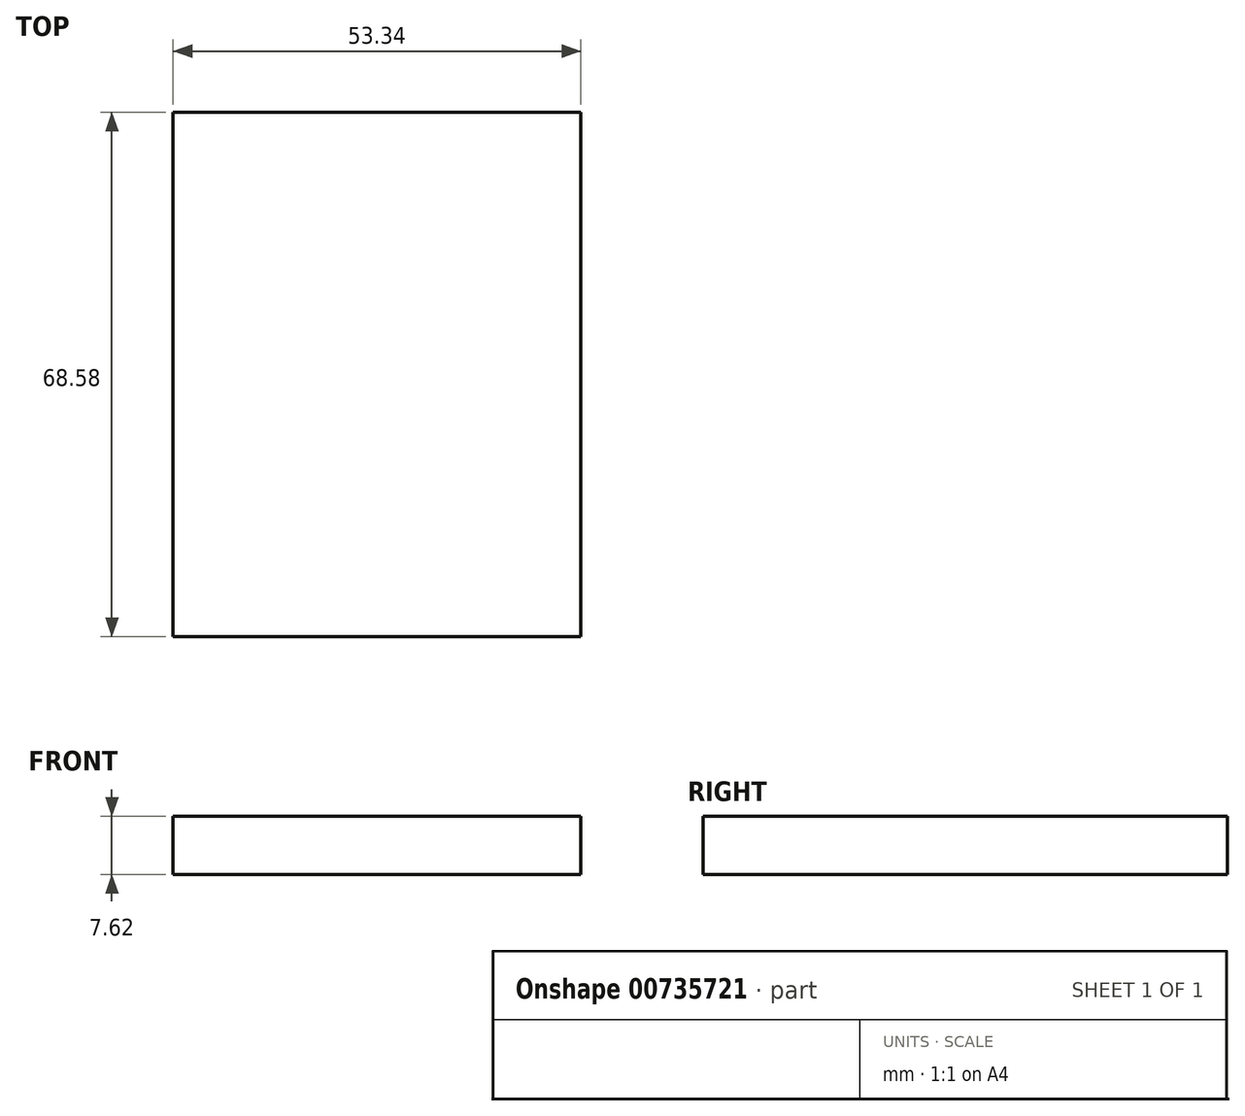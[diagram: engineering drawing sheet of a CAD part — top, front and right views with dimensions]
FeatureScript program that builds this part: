
annotation { "Feature Type Name" : "Feature", "Feature Type Description" : "" }
export const myFeature = defineFeature(function(context is Context, id is Id, definition is map)
    precondition{}
    {
        {
            var Q0;
            Q0=qCreatedBy(makeId("Top.planeOp"),FACE);
            var sketch = newSketch(context, id + "F0", { "sketchPlane" : qUnion([Q0])});
            skLineSegment(sketch, "E0", {"start": v(-26.67, 0) * mm, "end": v(0, 0) * mm});
            skLineSegment(sketch, "E1", {"start": v(0, 0) * mm, "end": v(0, 34.42) * mm});
            skLineSegment(sketch, "E2.MirrorCS", {"start": v(26.67, 0) * mm, "end": v(0, 0) * mm});
            skLineSegment(sketch, "E3.MirrorCS", {"start": v(0, 0) * mm, "end": v(0, -34.42) * mm});
            skLineSegment(sketch, "E4.bottom", {"start": v(-26.67, 34.42) * mm, "end": v(26.67, 34.42) * mm});
            skLineSegment(sketch, "E4.top", {"start": v(-26.67, -34.16) * mm, "end": v(26.67, -34.16) * mm});
            skLineSegment(sketch, "E4.left", {"start": v(-26.67, 34.42) * mm, "end": v(-26.67, -34.16) * mm});
            skLineSegment(sketch, "E4.right", {"start": v(26.67, 34.42) * mm, "end": v(26.67, -34.16) * mm});
            skSolve(sketch);
        }
        {
            var Q0;
            {var subQ0=sQuery(id+"F0.wireOp",EDGE,"E0");Q0=makeQuery(id+"F0.imprint","IMPRINT",FACE,{"disambiguationData":[TD([[makeQuery(id+"F0.imprint","IMPRINT",EDGE,{"derivedFrom":subQ0}),1.0]])]});}
            var Q1;
            {var subQ0=sQuery(id+"F0.wireOp",EDGE,"E1");Q1=makeQuery(id+"F0.imprint","IMPRINT",FACE,{"disambiguationData":[TD([[makeQuery(id+"F0.imprint","IMPRINT",EDGE,{"derivedFrom":subQ0}),-1.0]])]});}
            var Q2;
            {var subQ0=sQuery(id+"F0.wireOp",EDGE,"E0");Q2=makeQuery(id+"F0.imprint","IMPRINT",FACE,{"disambiguationData":[TD([[makeQuery(id+"F0.imprint","IMPRINT",EDGE,{"derivedFrom":subQ0}),-1.0]])]});}
            var Q3;
            {var subQ0=sQuery(id+"F0.wireOp",EDGE,"E2.MirrorCS");Q3=makeQuery(id+"F0.imprint","IMPRINT",FACE,{"disambiguationData":[TD([[makeQuery(id+"F0.imprint","IMPRINT",EDGE,{"derivedFrom":subQ0}),1.0]])]});}
            extrude(context, id + "F1", {"entities" : qUnion([Q0, Q1, Q2, Q3]), "depth" : 7.62 * mm, "offsetDistance" : 25.4 * mm});
        }
    });
